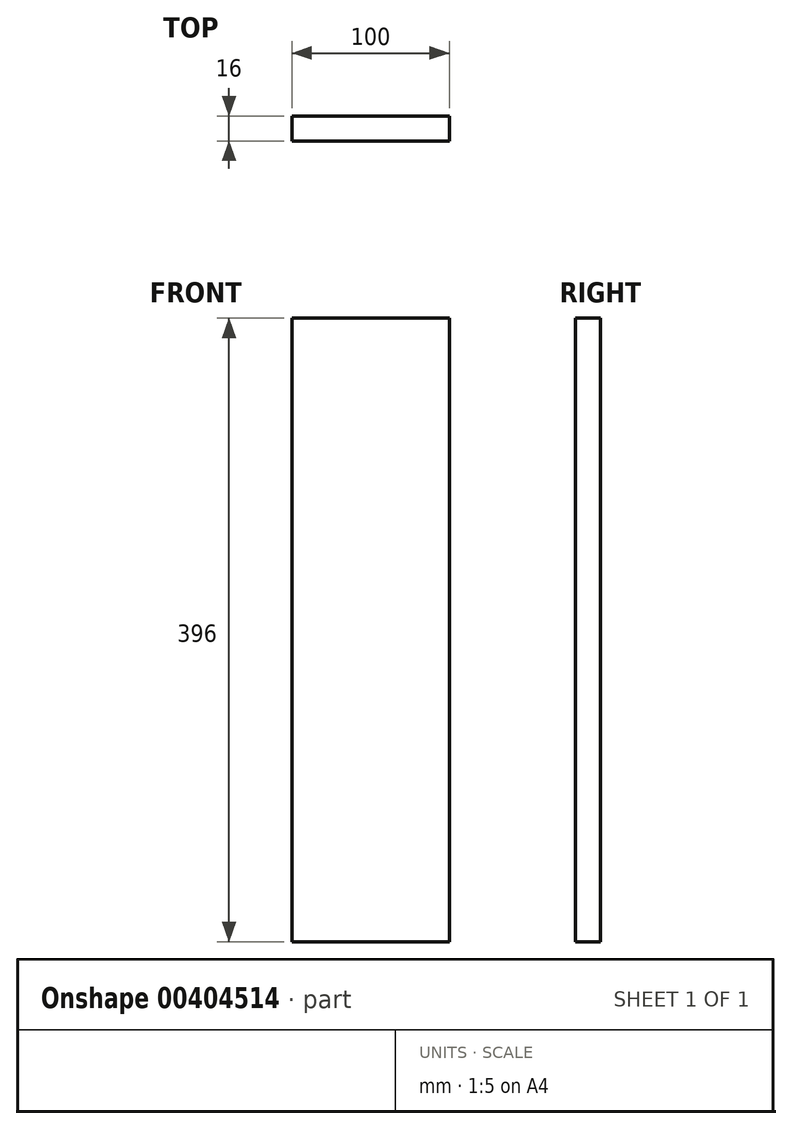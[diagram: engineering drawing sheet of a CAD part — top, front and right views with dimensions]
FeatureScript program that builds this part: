
annotation { "Feature Type Name" : "Feature", "Feature Type Description" : "" }
export const myFeature = defineFeature(function(context is Context, id is Id, definition is map)
    precondition{}
    {
        {
            var Q0;
            Q0=qCreatedBy(makeId("Front.planeOp"),FACE);
            var sketch = newSketch(context, id + "F0", { "sketchPlane" : qUnion([Q0])});
            skLineSegment(sketch, "E0.bottom", {"start": v(0, 0) * mm, "end": v(40.05, 0) * mm});
            skLineSegment(sketch, "E0.top", {"start": v(0, 44.02) * mm, "end": v(40.05, 44.02) * mm});
            skLineSegment(sketch, "E0.left", {"start": v(0, 0) * mm, "end": v(0, 44.02) * mm});
            skLineSegment(sketch, "E0.right", {"start": v(40.05, 0) * mm, "end": v(40.05, 44.02) * mm});
            skSolve(sketch);
        }
        {
            var Q0;
            Q0=makeQuery(id+"F0.imprint","IMPRINT",FACE,{"disambiguationData":[TD([[makeQuery(id+"F0.imprint","IMPRINT",EDGE,{"derivedFrom":sQuery(id+"F0.wireOp",EDGE,"E0.bottom")}),1.0]])]});
            extrude(context, id + "F1", {"entities" : qUnion([Q0]), "depth" : 25 * mm});
        }
        {
            var Q0;
            Q0=makeQuery(id+"F1.opExtrude","CAP_FACE",FACE,{"disambiguationData":[OSD([sQuery(id+"F0.wireOp",EDGE,"E0.bottom"),sQuery(id+"F0.wireOp",EDGE,"E0.top"),sQuery(id+"F0.wireOp",EDGE,"E0.left"),sQuery(id+"F0.wireOp",EDGE,"E0.right")])],"isStart":true});
            extrude(context, id + "F2", {"entities" : qUnion([Q0]), "operationType" : NewBodyOperationType.INTERSECT, "oppositeDirection" : true, "depth" : 16 * mm});
        }
        {
            var Q0;
            Q0=makeQuery(id+"F1.opExtrude","SWEPT_FACE",FACE,{"disambiguationData":[OSD([sQuery(id+"F0.wireOp",EDGE,"E0.left")])]});
            extrude(context, id + "F3", {"entities" : qUnion([Q0]), "operationType" : NewBodyOperationType.ADD, "oppositeDirection" : true, "depth" : 100 * mm});
        }
        {
            var Q0;
            {var subQ0=sQuery(id+"F0.wireOp",EDGE,"E0.bottom");Q0=makeQuery(id+"F3.boolean.opBoolean","MERGE",FACE,{"derivedFrom":[makeQuery(id+"F1.opExtrude","SWEPT_FACE",FACE,{"disambiguationData":[OSD([subQ0])]}),makeQuery(id+"F3.opExtrude","SWEPT_FACE",FACE,{"disambiguationData":[OSD([subQ0,sQuery(id+"F0.wireOp",EDGE,"E0.left")])]})]});}
            extrude(context, id + "F4", {"entities" : qUnion([Q0]), "operationType" : NewBodyOperationType.ADD, "oppositeDirection" : true, "depth" : 1996 * mm});
        }
        {
            var Q0;
            {var subQ0=sQuery(id+"F0.wireOp",EDGE,"E0.bottom");Q0=makeQuery(id+"F3.boolean.opBoolean","MERGE",FACE,{"derivedFrom":[makeQuery(id+"F1.opExtrude","SWEPT_FACE",FACE,{"disambiguationData":[OSD([subQ0])]}),makeQuery(id+"F3.opExtrude","SWEPT_FACE",FACE,{"disambiguationData":[OSD([subQ0,sQuery(id+"F0.wireOp",EDGE,"E0.left")])]})]});}
            extrude(context, id + "F5", {"entities" : qUnion([Q0]), "operationType" : NewBodyOperationType.INTERSECT, "oppositeDirection" : true, "depth" : 396 * mm});
        }
    });
